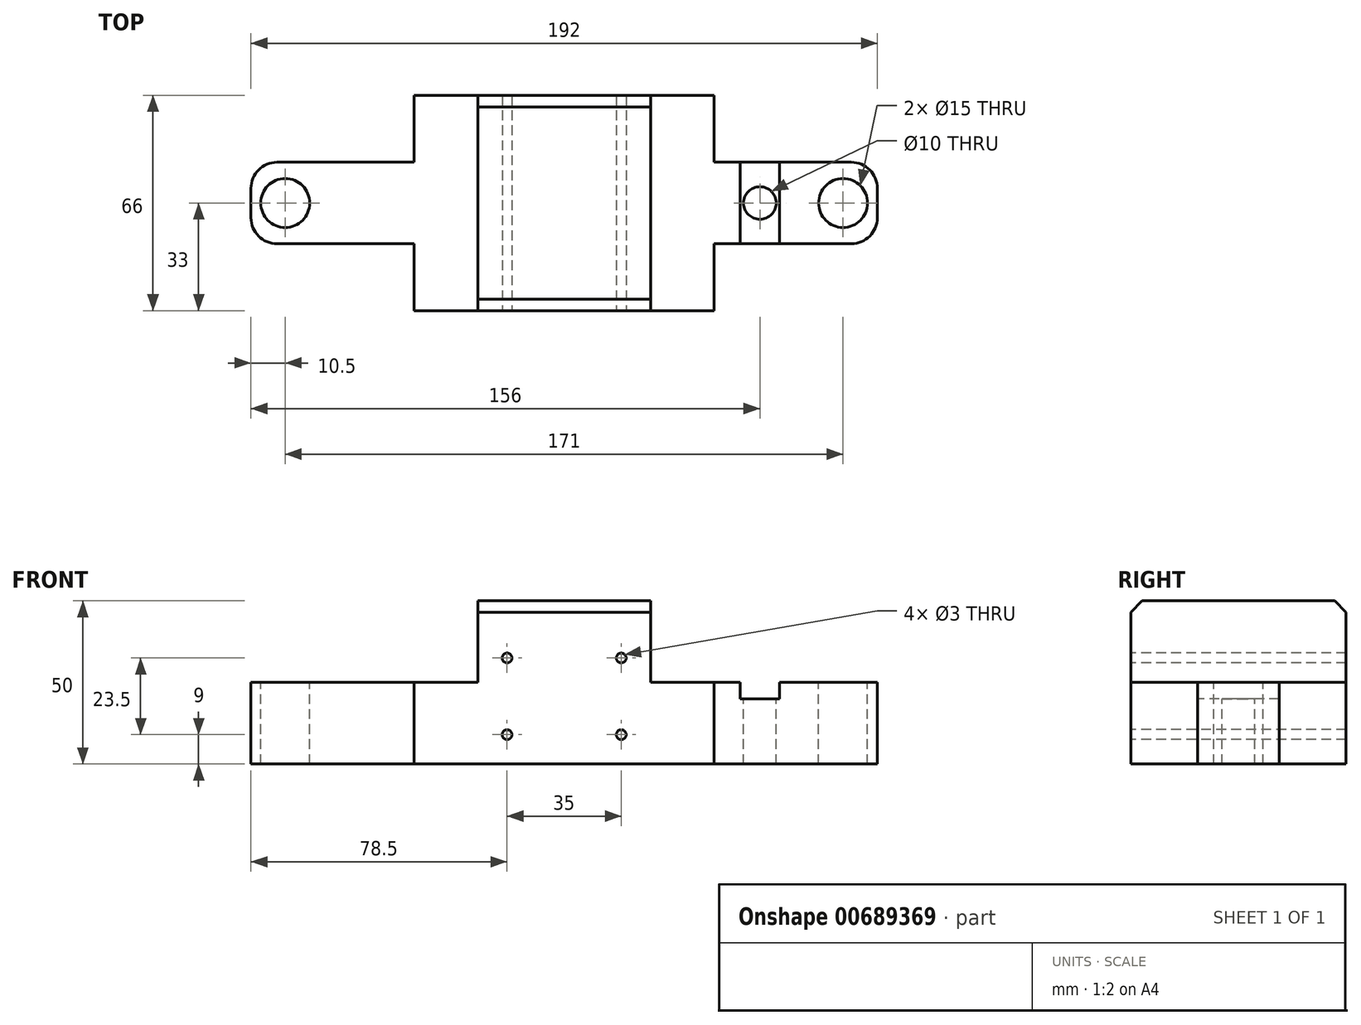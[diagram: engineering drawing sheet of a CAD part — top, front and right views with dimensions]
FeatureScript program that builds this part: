
annotation { "Feature Type Name" : "Feature", "Feature Type Description" : "" }
export const myFeature = defineFeature(function(context is Context, id is Id, definition is map)
    precondition{}
    {
        {
            var Q0;
            Q0=qCreatedBy(makeId("Front.planeOp"),FACE);
            var sketch = newSketch(context, id + "F0", { "sketchPlane" : qUnion([Q0])});
            skLineSegment(sketch, "E0", {"start": v(0, 0) * mm, "end": v(92, 0) * mm});
            skLineSegment(sketch, "E1", {"start": v(92, 0) * mm, "end": v(92, 25) * mm});
            skLineSegment(sketch, "E2", {"start": v(72.5, 50) * mm, "end": v(19.5, 50) * mm});
            skLineSegment(sketch, "E3", {"start": v(92, 25) * mm, "end": v(72.5, 25) * mm});
            skLineSegment(sketch, "E4", {"start": v(72.5, 25) * mm, "end": v(72.5, 50) * mm});
            skLineSegment(sketch, "E5", {"start": v(0, 0) * mm, "end": v(0, 25) * mm});
            skLineSegment(sketch, "E6", {"start": v(19.5, 50) * mm, "end": v(19.5, 25) * mm});
            skLineSegment(sketch, "E7", {"start": v(19.5, 25) * mm, "end": v(0, 25) * mm});
            skSolve(sketch);
        }
        {
            var Q0;
            Q0=qSketchRegion(id+"F0",true);
            extrude(context, id + "F1", {"entities" : qUnion([Q0]), "depth" : 66 * mm});
        }
        {
            var Q0;
            Q0=makeQuery(id+"F1.opExtrude","SWEPT_FACE",FACE,{"disambiguationData":[OSD([sQuery(id+"F0.wireOp",EDGE,"E4")])]});
            var sketch = newSketch(context, id + "F2", { "sketchPlane" : qUnion([Q0])});
            skLineSegment(sketch, "E8", {"start": v(-66, 50) * mm, "end": v(-62.5, 50) * mm});
            skLineSegment(sketch, "E9", {"start": v(-62.5, 50) * mm, "end": v(-66, 46.5) * mm});
            skLineSegment(sketch, "E10", {"start": v(-66, 50) * mm, "end": v(-66, 46.5) * mm});
            skPoint(sketch, "E11.orphan", {"position": v(-66, 37.5) * mm});
            skLineSegment(sketch, "E12", {"start": v(0, 50) * mm, "end": v(-3.5, 50) * mm});
            skLineSegment(sketch, "E13", {"start": v(-3.5, 50) * mm, "end": v(0, 46.5) * mm});
            skLineSegment(sketch, "E14", {"start": v(0, 50) * mm, "end": v(0, 46.5) * mm});
            skPoint(sketch, "E15.orphan", {"position": v(0, 37.5) * mm});
            skSolve(sketch);
        }
        {
            var Q0;
            Q0=qSketchRegion(id+"F2",true);
            extrude(context, id + "F3", {"entities" : qUnion([Q0]), "operationType" : NewBodyOperationType.REMOVE, "endBound" : BoundingType.THROUGH_ALL, "oppositeDirection" : true, "depth" : 25 * mm});
        }
        {
            var Q0;
            Q0=makeQuery(id+"F1.opExtrude","SWEPT_FACE",FACE,{"disambiguationData":[OSD([sQuery(id+"F0.wireOp",EDGE,"E1")])]});
            var sketch = newSketch(context, id + "F4", { "sketchPlane" : qUnion([Q0])});
            skLineSegment(sketch, "E16", {"start": v(-45.5, 0) * mm, "end": v(-20.5, 0) * mm});
            skLineSegment(sketch, "E17", {"start": v(-45.5, 0) * mm, "end": v(-45.5, 25) * mm});
            skLineSegment(sketch, "E18", {"start": v(-45.5, 25) * mm, "end": v(-20.5, 25) * mm});
            skLineSegment(sketch, "E19", {"start": v(-20.5, 0) * mm, "end": v(-20.5, 25) * mm});
            skSolve(sketch);
        }
        {
            var Q0;
            Q0=qSketchRegion(id+"F4",true);
            extrude(context, id + "F5", {"entities" : qUnion([Q0]), "operationType" : NewBodyOperationType.ADD, "depth" : 50 * mm, "hasSecondDirection" : true, "secondDirectionOppositeDirection" : true, "secondDirectionDepth" : 142 * mm});
        }
        {
            var Q0;
            Q0=makeQuery(id+"F5.boolean.opBoolean","MERGE",FACE,{"derivedFrom":[makeQuery(id+"F1.opExtrude","SWEPT_FACE",FACE,{"disambiguationData":[OSD([sQuery(id+"F0.wireOp",EDGE,"E3")])]}),makeQuery(id+"F5.opExtrude","SWEPT_FACE",FACE,{"disambiguationData":[OSD([sQuery(id+"F4.wireOp",EDGE,"E18")])]})]});
            var sketch = newSketch(context, id + "F6", { "sketchPlane" : qUnion([Q0])});
            skCircle(sketch, "E20", {"center": v(131.5, -33) * mm, "radius": 7.5 * mm});
            skCircle(sketch, "E21", {"center": v(-39.5, -33) * mm, "radius": 7.5 * mm});
            skSolve(sketch);
        }
        {
            var Q0;
            Q0=qSketchRegion(id+"F6",true);
            extrude(context, id + "F7", {"entities" : qUnion([Q0]), "operationType" : NewBodyOperationType.REMOVE, "endBound" : BoundingType.THROUGH_ALL, "oppositeDirection" : true, "depth" : 25 * mm});
        }
        {
            var Q0;
            Q0=makeQuery(id+"F5.boolean.opBoolean","MERGE",FACE,{"derivedFrom":[makeQuery(id+"F1.opExtrude","SWEPT_FACE",FACE,{"disambiguationData":[OSD([sQuery(id+"F0.wireOp",EDGE,"E3")])]}),makeQuery(id+"F5.opExtrude","SWEPT_FACE",FACE,{"disambiguationData":[OSD([sQuery(id+"F4.wireOp",EDGE,"E18")])]})]});
            var sketch = newSketch(context, id + "F8", { "sketchPlane" : qUnion([Q0])});
            skCircle(sketch, "E22", {"center": v(106, -33) * mm, "radius": 5 * mm});
            skSolve(sketch);
        }
        {
            var Q0;
            Q0=qSketchRegion(id+"F8",true);
            extrude(context, id + "F9", {"entities" : qUnion([Q0]), "operationType" : NewBodyOperationType.REMOVE, "oppositeDirection" : true, "depth" : 25 * mm, "offsetDistance" : 25 * mm});
        }
        {
            var Q0;
            Q0=makeQuery(id+"F5.opExtrude","CAP_EDGE",EDGE,{"disambiguationData":[OSD([sQuery(id+"F4.wireOp",EDGE,"E19")])],"isStart":false});
            var Q1;
            Q1=makeQuery(id+"F5.opExtrude","CAP_EDGE",EDGE,{"disambiguationData":[OSD([sQuery(id+"F4.wireOp",EDGE,"E17")])],"isStart":false});
            var Q2;
            Q2=makeQuery(id+"F5.opExtrude","CAP_EDGE",EDGE,{"disambiguationData":[OSD([sQuery(id+"F4.wireOp",EDGE,"E17")])],"isStart":true});
            var Q3;
            Q3=makeQuery(id+"F5.opExtrude","CAP_EDGE",EDGE,{"disambiguationData":[OSD([sQuery(id+"F4.wireOp",EDGE,"E19")])],"isStart":true});
            fillet(context, id + "F10", {"entities" : qUnion([Q0, Q1, Q2, Q3]), "radius" : 8 * mm, "tangentPropagation" : true, "allowEdgeOverflow" : false});
        }
        {
            var Q0;
            Q0=makeQuery(id+"F5.boolean.opBoolean","MERGE",FACE,{"derivedFrom":[makeQuery(id+"F1.opExtrude","SWEPT_FACE",FACE,{"disambiguationData":[OSD([sQuery(id+"F0.wireOp",EDGE,"E3")])]}),makeQuery(id+"F5.opExtrude","SWEPT_FACE",FACE,{"disambiguationData":[OSD([sQuery(id+"F4.wireOp",EDGE,"E18")])]})]});
            var sketch = newSketch(context, id + "F11", { "sketchPlane" : qUnion([Q0])});
            skLineSegment(sketch, "E23", {"start": v(112, -20.5) * mm, "end": v(112, -45.5) * mm});
            skLineSegment(sketch, "E24", {"start": v(100, -20.5) * mm, "end": v(100, -45.5) * mm});
            skLineSegment(sketch, "E25", {"start": v(100, -20.5) * mm, "end": v(112, -20.5) * mm});
            skLineSegment(sketch, "E26", {"start": v(112, -45.5) * mm, "end": v(100, -45.5) * mm});
            skSolve(sketch);
        }
        {
            var Q0;
            Q0=qSketchRegion(id+"F11",true);
            extrude(context, id + "F12", {"entities" : qUnion([Q0]), "operationType" : NewBodyOperationType.REMOVE, "oppositeDirection" : true, "depth" : 5 * mm, "offsetDistance" : 25 * mm});
        }
        {
            var Q0;
            Q0=makeQuery(id+"F1.opExtrude","CAP_FACE",FACE,{"disambiguationData":[OSD([sQuery(id+"F0.wireOp",EDGE,"E0"),sQuery(id+"F0.wireOp",EDGE,"E1"),sQuery(id+"F0.wireOp",EDGE,"E2"),sQuery(id+"F0.wireOp",EDGE,"E3"),sQuery(id+"F0.wireOp",EDGE,"E4"),sQuery(id+"F0.wireOp",EDGE,"E5"),sQuery(id+"F0.wireOp",EDGE,"E6"),sQuery(id+"F0.wireOp",EDGE,"E7")])],"isStart":false});
            var sketch = newSketch(context, id + "F13", { "sketchPlane" : qUnion([Q0])});
            skPoint(sketch, "E27", {"position": v(28.5, 32.5) * mm});
            skPoint(sketch, "E28", {"position": v(63.5, 32.5) * mm});
            skPoint(sketch, "E29", {"position": v(63.5, 9) * mm});
            skPoint(sketch, "E30", {"position": v(28.5, 9) * mm});
            skSolve(sketch);
        }
        {
            var Q0;
            Q0=sQuery(id+"F13.wireOp",VERTEX,"E27");
            var Q1;
            Q1=sQuery(id+"F13.wireOp",VERTEX,"E28");
            var Q2;
            Q2=sQuery(id+"F13.wireOp",VERTEX,"E29");
            var Q3;
            Q3=sQuery(id+"F13.wireOp",VERTEX,"E30");
            var Q4;
            Q4=makeQuery(id+"F1.opExtrude","SWEPT_BODY",BODY,{"disambiguationData":[OSD([sQuery(id+"F0.wireOp",EDGE,"E0"),sQuery(id+"F0.wireOp",EDGE,"E1"),sQuery(id+"F0.wireOp",EDGE,"E2"),sQuery(id+"F0.wireOp",EDGE,"E3"),sQuery(id+"F0.wireOp",EDGE,"E4"),sQuery(id+"F0.wireOp",EDGE,"E5"),sQuery(id+"F0.wireOp",EDGE,"E6"),sQuery(id+"F0.wireOp",EDGE,"E7")])]});
            hole(context, id + "F14", {"style" : HoleStyle.SIMPLE, "endStyle" : HoleEndStyle.THROUGH, "holeDiameter" : 3 * mm, "majorDiameter" : 5 * mm, "isTappedThrough" : true, "tappedDepth" : 12 * mm, "tapClearance" : 3, "startFromSketch" : true, "locations" : qUnion([Q0, Q1, Q2, Q3]), "scope" : qUnion([Q4])});
        }
    });
